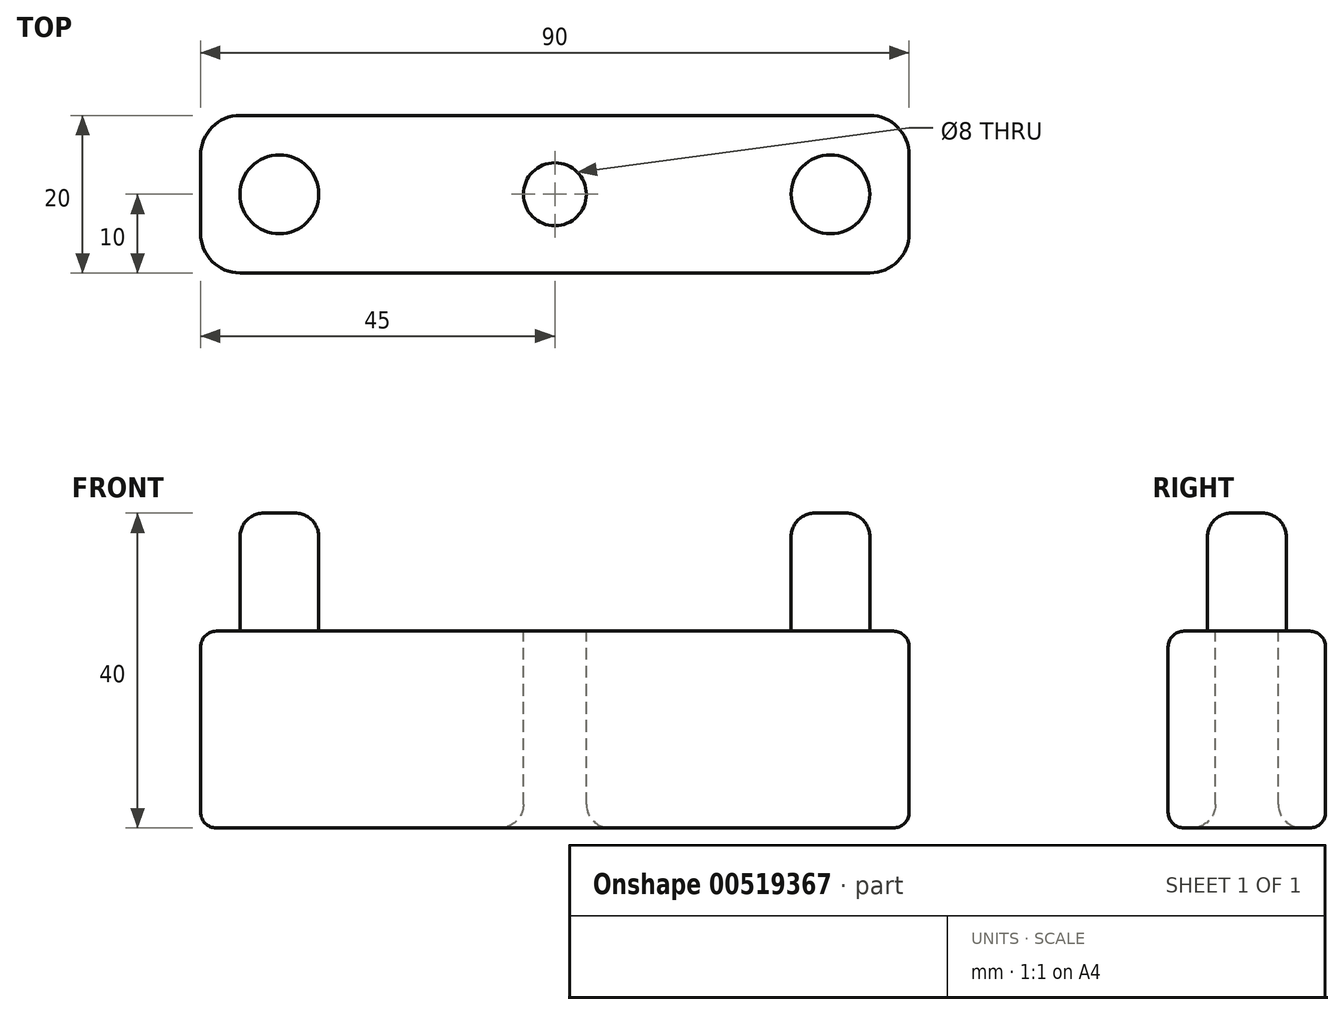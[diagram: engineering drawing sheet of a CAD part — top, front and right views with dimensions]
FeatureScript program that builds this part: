
annotation { "Feature Type Name" : "Feature", "Feature Type Description" : "" }
export const myFeature = defineFeature(function(context is Context, id is Id, definition is map)
    precondition{}
    {
        {
            var Q0;
            Q0=qCreatedBy(makeId("Top.planeOp"),FACE);
            var sketch = newSketch(context, id + "F0", { "sketchPlane" : qUnion([Q0])});
            skLineSegment(sketch, "E0.bottom", {"start": v(0, 0) * mm, "end": v(90, 0) * mm});
            skLineSegment(sketch, "E0.top", {"start": v(0, 20) * mm, "end": v(90, 20) * mm});
            skLineSegment(sketch, "E0.left", {"start": v(0, 0) * mm, "end": v(0, 20) * mm});
            skLineSegment(sketch, "E0.right", {"start": v(90, 0) * mm, "end": v(90, 20) * mm});
            skSolve(sketch);
        }
        {
            var Q0;
            Q0=makeQuery(id+"F0.imprint","IMPRINT",FACE,{"disambiguationData":[TD([[makeQuery(id+"F0.imprint","IMPRINT",EDGE,{"derivedFrom":sQuery(id+"F0.wireOp",EDGE,"E0.bottom")}),1.0]])]});
            extrude(context, id + "F1", {"entities" : qUnion([Q0]), "oppositeDirection" : true, "depth" : 25 * mm, "offsetDistance" : 25 * mm});
        }
        {
            var Q0;
            Q0=qCreatedBy(makeId("Top.planeOp"),FACE);
            var sketch = newSketch(context, id + "F2", { "sketchPlane" : qUnion([Q0])});
            skCircle(sketch, "E1", {"center": v(80, 10) * mm, "radius": 5 * mm});
            skCircle(sketch, "E2", {"center": v(10, 10) * mm, "radius": 5 * mm});
            skSolve(sketch);
        }
        {
            var Q0;
            Q0=makeQuery(id+"F2.imprint","IMPRINT",FACE,{"disambiguationData":[TD([[makeQuery(id+"F2.imprint","IMPRINT",EDGE,{"derivedFrom":sQuery(id+"F2.wireOp",EDGE,"E2")}),1.0]])]});
            var Q1;
            Q1=makeQuery(id+"F2.imprint","IMPRINT",FACE,{"disambiguationData":[TD([[makeQuery(id+"F2.imprint","IMPRINT",EDGE,{"derivedFrom":sQuery(id+"F2.wireOp",EDGE,"E1")}),1.0]])]});
            extrude(context, id + "F3", {"entities" : qUnion([Q0, Q1]), "operationType" : NewBodyOperationType.ADD, "depth" : 15 * mm, "offsetDistance" : 25 * mm});
        }
        {
            var Q0;
            Q0=qCreatedBy(makeId("Top.planeOp"),FACE);
            var sketch = newSketch(context, id + "F4", { "sketchPlane" : qUnion([Q0])});
            skCircle(sketch, "E3", {"center": v(45, 10) * mm, "radius": 4 * mm});
            skSolve(sketch);
        }
        {
            var Q0;
            Q0 = qSketchRegion(id + "F4", true);
            extrude(context, id + "F5", {"entities" : qUnion([Q0]), "operationType" : NewBodyOperationType.REMOVE, "endBound" : BoundingType.THROUGH_ALL, "oppositeDirection" : true, "depth" : 25 * mm, "offsetDistance" : 25 * mm});
        }
        {
            var Q0;
            Q0=makeQuery(id+"F1.opExtrude","SWEPT_EDGE",EDGE,{"disambiguationData":[OSD([sQuery(id+"F0.wireOp",EDGE,"E0.bottom"),sQuery(id+"F0.wireOp",EDGE,"E0.left")])]});
            var Q1;
            Q1=makeQuery(id+"F1.opExtrude","SWEPT_EDGE",EDGE,{"disambiguationData":[OSD([sQuery(id+"F0.wireOp",EDGE,"E0.top"),sQuery(id+"F0.wireOp",EDGE,"E0.left")])]});
            var Q2;
            Q2=makeQuery(id+"F1.opExtrude","SWEPT_EDGE",EDGE,{"disambiguationData":[OSD([sQuery(id+"F0.wireOp",EDGE,"E0.bottom"),sQuery(id+"F0.wireOp",EDGE,"E0.right")])]});
            var Q3;
            Q3=makeQuery(id+"F1.opExtrude","SWEPT_EDGE",EDGE,{"disambiguationData":[OSD([sQuery(id+"F0.wireOp",EDGE,"E0.top"),sQuery(id+"F0.wireOp",EDGE,"E0.right")])]});
            fillet(context, id + "F6", {"entities" : qUnion([Q0, Q1, Q2, Q3]), "radius" : 5 * mm, "tangentPropagation" : true, "allowEdgeOverflow" : false});
        }
        {
            var Q0;
            Q0=makeQuery(id+"F3.opExtrude","CAP_EDGE",EDGE,{"disambiguationData":[OSD([sQuery(id+"F2.wireOp",EDGE,"E2")])],"isStart":false});
            var Q1;
            Q1=makeQuery(id+"F3.opExtrude","CAP_EDGE",EDGE,{"disambiguationData":[OSD([sQuery(id+"F2.wireOp",EDGE,"E1")])],"isStart":false});
            fillet(context, id + "F7", {"entities" : qUnion([Q0, Q1]), "radius" : 3 * mm, "tangentPropagation" : true, "allowEdgeOverflow" : false});
        }
        {
            var Q0;
            Q0=makeQuery(id+"F5.boolean.opBoolean","INTERSECT",EDGE,{"derivedFrom":[makeQuery(id+"F1.opExtrude","CAP_FACE",FACE,{"disambiguationData":[OSD([sQuery(id+"F0.wireOp",EDGE,"E0.bottom"),sQuery(id+"F0.wireOp",EDGE,"E0.top"),sQuery(id+"F0.wireOp",EDGE,"E0.left"),sQuery(id+"F0.wireOp",EDGE,"E0.right")])],"isStart":false}),makeQuery(id+"F5.opExtrude","SWEPT_FACE",FACE,{"disambiguationData":[OSD([sQuery(id+"F4.wireOp",EDGE,"E3")])]})]});
            fillet(context, id + "F8", {"entities" : qUnion([Q0]), "radius" : 3 * mm, "tangentPropagation" : true, "allowEdgeOverflow" : false});
        }
        {
            var Q0;
            Q0=makeQuery(id+"F1.opExtrude","CAP_EDGE",EDGE,{"disambiguationData":[OSD([sQuery(id+"F0.wireOp",EDGE,"E0.bottom")])],"isStart":false});
            fillet(context, id + "F9", {"entities" : qUnion([Q0]), "radius" : 2 * mm, "tangentPropagation" : true, "allowEdgeOverflow" : false});
        }
        {
            var Q0;
            Q0=makeQuery(id+"F1.opExtrude","CAP_EDGE",EDGE,{"disambiguationData":[OSD([sQuery(id+"F0.wireOp",EDGE,"E0.bottom")])],"isStart":true});
            fillet(context, id + "F10", {"entities" : qUnion([Q0]), "radius" : 2 * mm, "tangentPropagation" : true, "allowEdgeOverflow" : false});
        }
    });
